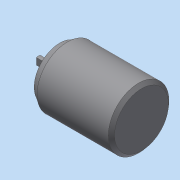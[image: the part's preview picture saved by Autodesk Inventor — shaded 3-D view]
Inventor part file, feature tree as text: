
AUTODESK INVENTOR PART (.ipt)
format: ipt  version: 2017 (Build 210142000, 142)  size: 143,360 bytes
history: native  units: in
note: dims shown in document units (in); Inventor stores cm internally (conversion verified against a paired STEP export)
features: sketch x4, extrude x3, other x1, plane x1
ambient origin geometry x8: Origin, YZ Plane, XZ Plane, XY Plane, X Axis, Y Axis, Z Axis, Center Point
bodies: Body1 (feature_tree)
feature tree (9):
  other  "motor body"
  extrude  "axis slot"  Depth=0.315in
  extrude  "mounting holes"  Depth=0.1575in
  plane  "Work Plane1"
  extrude  "cable hole"  Depth=1.1024in
  sketch  "Sketch1"  dims[d7=0.8858in d9=0.315in]
  sketch  "Sketch4"  dims[d10=2.9134in d14=0.1575in]
  sketch  "Sketch5"  dims[d16=1.2402in d17=1.1024in]
  sketch  "Sketch6"  dims[d18=0.8661in d19=90.0deg d20=0.9843in d21=0.0in d22=0.125in d23=0.7874in d25=1.2205in d26=0.7874in d28=1.2205in d31=0.6102in d32=0.6102in d33=0.1575in d34=0.0in d35=0.7874in d36=0.2165in d37=0.0591in d38=0.3937in d39=0.0in d40=3.3465in]
